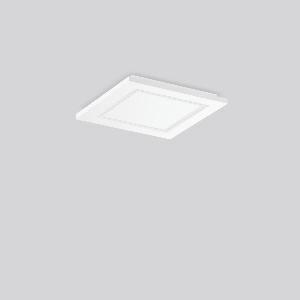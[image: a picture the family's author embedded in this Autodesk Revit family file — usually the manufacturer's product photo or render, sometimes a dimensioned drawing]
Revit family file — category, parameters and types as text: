
# Revit family: hemis_square_312188_002_a447
name_source: partatom
category: Lighting Fixtures
units: mm (PartAtom-declared; Revit-internal decimal feet)

## family parameters
Cut with Voids When Loaded = No
Host = Face
Light Source = No
Part Type = Normal
Room Calculation Point = No
Round Connector Dimension = Use Diameter
Shared = No

## types (1)
- HEMIS square (1 x LED Modul 830, 1700 lm, 3000)
    Apparent Load = 15 VA
    CIE Flux Codes = 85 99 100 100 100
    Color Rendering = 80
    Color Temperature = 3000
    Default Elevation = 1800 mm
    Description = Series: HEMIS square
Glare-free LED ceiling luminaire with optical lens system. Base: metal, powder-coated, with bayonet fixing. Housing: plastic (polycarbonate). Housing and diffuser are screwed together. Diffuser with optic lenses. Big terminal block; ideal for through-wiring. Sealing strip on the back of the luminaire connects seamlessly with the ceiling. Easy installation with Plug+Play plug connection. Thanks to RUG < 22 ideal for corridors, stairways, shops, schools, meeting rooms, rest areas. 
Colour: white
Length: 300 mm
Width: 300 mm
Height: 33 mm
Lamp: LED
Socket: without socket
Colour temperature: 3000K
Colour rendering index (CRI): 80
System power: 15 W
Rated luminous flux: 1700 lm
Luminous efficiency: 113 lm/W
Control gear: Regulated power supply
Protection class: I
Type of protection: IP 40
    Height = 33 mm
    Lamp = 1 x LED Modul 830
    Lamp Light Flux = 1700 lm
    Lamp count = 1
    Length = 300 mm
    Lifetime = 50000 h
    Luminous efficacy = 113 lm/W
    Manufacturer = RZB
    ModVariant = No
    Model = 312188.002
    Mounting Place = Ceiling
    Mounting Type = Surface mounted
    Number of Poles = 1
    OnlyDefault = Yes
    Power Factor = 1
    Product Name = HEMIS square
    Product group = Surface mounted modular luminaires
    ProductGroupID = 306
    Protection Class = Protection class I
    Protection Degree = IP 40
    RLX_Detail_Level = 1
    RLX_Emergency_Light_Flux = 0 lm
    RLX_Emergency_Type = 0
    RLX_Emergency_Type_DB = No
    RlxData = <blob elided: 12641 chars, md5=b35acc8b>
    Socket = socket
    Standby Power = 0 W
    System Light Flux = 1700 lm
    System Power = 15 W
    Type Comments = Product without accessories
    Type Image = 312188.002.jpg
    URL = http://relux.com
    VarID = ---
    Voltage = 230 V
    Voltage Range = 220-240 V
    Weight = 0.00 kg
    Width = 300 mm

## geometry (parser evidence)
native form markers: Sweep x9
no freeform markers — native parametric forms only
